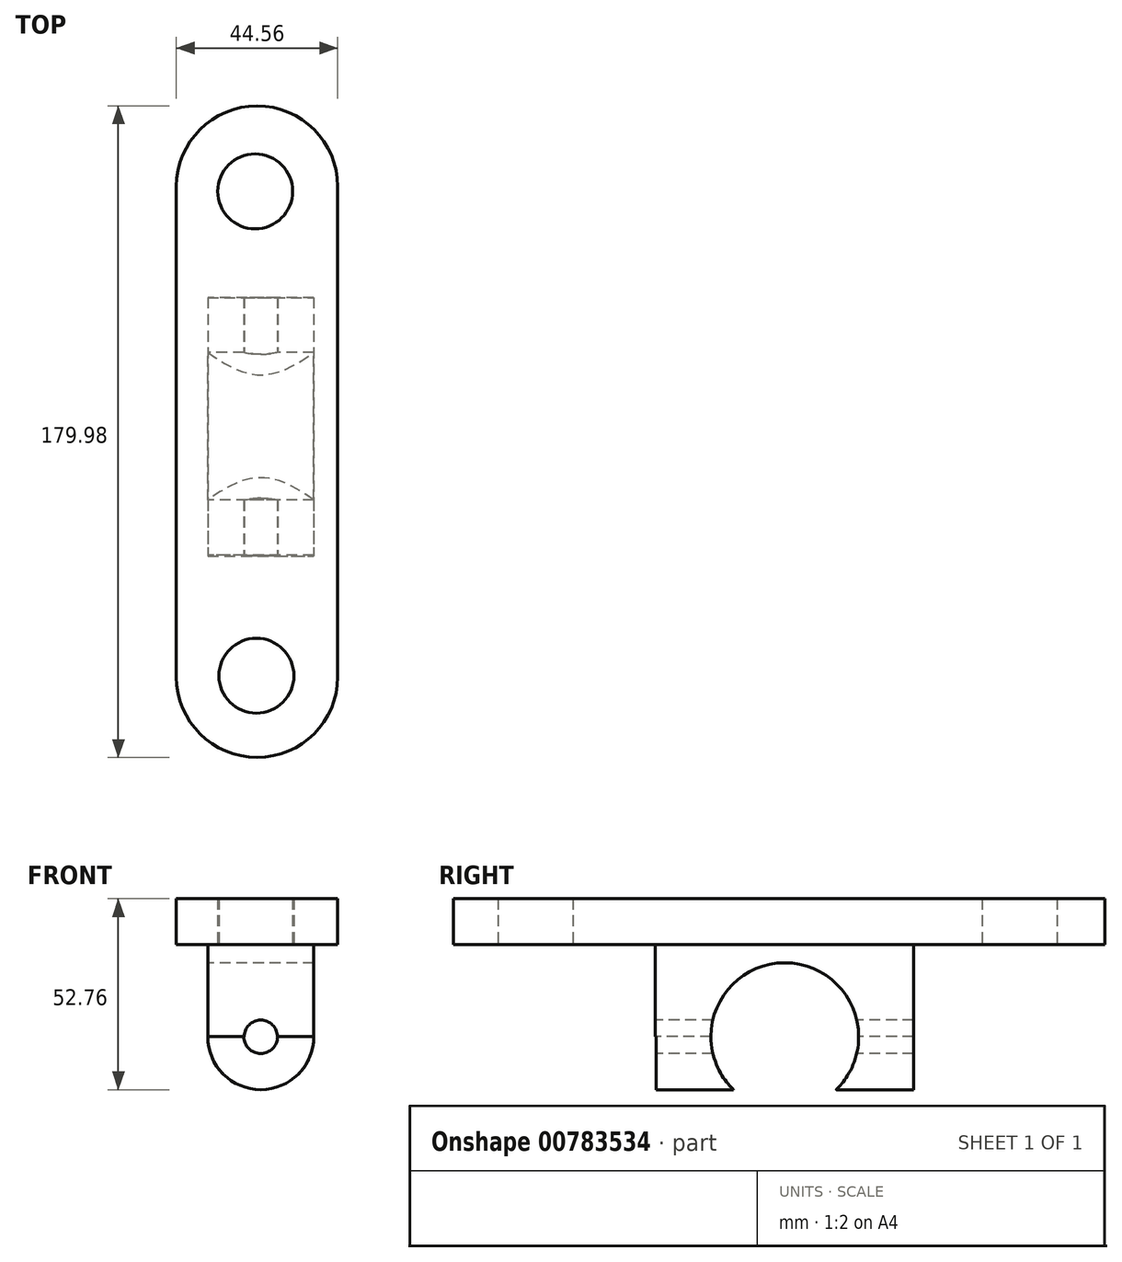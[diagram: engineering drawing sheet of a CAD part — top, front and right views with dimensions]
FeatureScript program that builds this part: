
annotation { "Feature Type Name" : "Feature", "Feature Type Description" : "" }
export const myFeature = defineFeature(function(context is Context, id is Id, definition is map)
    precondition{}
    {
        {
            var Q0;
            Q0=qCreatedBy(makeId("Top.planeOp"),FACE);
            var sketch = newSketch(context, id + "F0", { "sketchPlane" : qUnion([Q0])});
            skLineSegment(sketch, "E0.bottom", {"start": v(-28.13, -64.81) * mm, "end": v(16.43, -64.81) * mm});
            skLineSegment(sketch, "E0.top", {"start": v(-28.13, 70.6) * mm, "end": v(16.43, 70.6) * mm});
            skLineSegment(sketch, "E0.left", {"start": v(-28.13, -64.81) * mm, "end": v(-28.13, 70.6) * mm});
            skLineSegment(sketch, "E0.right", {"start": v(16.43, -64.81) * mm, "end": v(16.43, 70.6) * mm});
            skCircle(sketch, "E1", {"center": v(-5.85, 70.6) * mm, "radius": 22.28 * mm});
            skCircle(sketch, "E2", {"center": v(-5.85, -64.81) * mm, "radius": 22.28 * mm});
            skSolve(sketch);
        }
        {
            var Q0;
            {var subQ0=sQuery(id+"F0.wireOp",EDGE,"E0.left");Q0=makeQuery(id+"F0.imprint","IMPRINT",FACE,{"disambiguationData":[TD([[makeQuery(id+"F0.imprint","IMPRINT",EDGE,{"derivedFrom":subQ0}),-1.0]])]});}
            var Q1;
            {var subQ0=sQuery(id+"F0.wireOp",EDGE,"E0.top");Q1=makeQuery(id+"F0.imprint","IMPRINT",FACE,{"disambiguationData":[TD([[makeQuery(id+"F0.imprint","IMPRINT",EDGE,{"derivedFrom":subQ0}),-1.0]])]});}
            var Q2;
            {var subQ0=sQuery(id+"F0.wireOp",EDGE,"E0.top");Q2=makeQuery(id+"F0.imprint","IMPRINT",FACE,{"disambiguationData":[TD([[makeQuery(id+"F0.imprint","IMPRINT",EDGE,{"derivedFrom":subQ0}),1.0]])]});}
            var Q3;
            {var subQ0=sQuery(id+"F0.wireOp",EDGE,"E0.bottom");Q3=makeQuery(id+"F0.imprint","IMPRINT",FACE,{"disambiguationData":[TD([[makeQuery(id+"F0.imprint","IMPRINT",EDGE,{"derivedFrom":subQ0}),-1.0]])]});}
            var Q4;
            {var subQ0=sQuery(id+"F0.wireOp",EDGE,"E0.bottom");Q4=makeQuery(id+"F0.imprint","IMPRINT",FACE,{"disambiguationData":[TD([[makeQuery(id+"F0.imprint","IMPRINT",EDGE,{"derivedFrom":subQ0}),1.0]])]});}
            extrude(context, id + "F1", {"entities" : qUnion([Q0, Q1, Q2, Q3, Q4]), "depth" : 12.7 * mm, "offsetDistance" : 25.4 * mm});
        }
        {
            var Q0;
            Q0=qCreatedBy(makeId("Top.planeOp"),FACE);
            var sketch = newSketch(context, id + "F2", { "sketchPlane" : qUnion([Q0])});
            skCircle(sketch, "E3", {"center": v(-6.38, 69.27) * mm, "radius": 10.35 * mm});
            skCircle(sketch, "E4", {"center": v(-6.03, -64.52) * mm, "radius": 10.35 * mm});
            skSolve(sketch);
        }
        {
            var Q0;
            Q0=makeQuery(id+"F2.imprint","IMPRINT",FACE,{"disambiguationData":[TD([[makeQuery(id+"F2.imprint","IMPRINT",EDGE,{"derivedFrom":sQuery(id+"F2.wireOp",EDGE,"E3")}),1.0]])]});
            var Q1;
            Q1=makeQuery(id+"F2.imprint","IMPRINT",FACE,{"disambiguationData":[TD([[makeQuery(id+"F2.imprint","IMPRINT",EDGE,{"derivedFrom":sQuery(id+"F2.wireOp",EDGE,"E4")}),1.0]])]});
            extrude(context, id + "F3", {"entities" : qUnion([Q0, Q1]), "operationType" : NewBodyOperationType.REMOVE, "depth" : 12.7 * mm, "offsetDistance" : 25.4 * mm});
        }
        {
            var Q0;
            Q0=qCreatedBy(makeId("Top.planeOp"),FACE);
            var sketch = newSketch(context, id + "F4", { "sketchPlane" : qUnion([Q0])});
            skLineSegment(sketch, "E5.bottom", {"start": v(-19.48, 39.96) * mm, "end": v(9.83, 39.96) * mm});
            skLineSegment(sketch, "E5.top", {"start": v(-19.48, -31.42) * mm, "end": v(9.83, -31.42) * mm});
            skLineSegment(sketch, "E5.left", {"start": v(-19.48, 39.96) * mm, "end": v(-19.48, -31.42) * mm});
            skLineSegment(sketch, "E5.right", {"start": v(9.83, 39.96) * mm, "end": v(9.83, -31.42) * mm});
            skSolve(sketch);
        }
        {
            var Q0;
            Q0=makeQuery(id+"F4.imprint","IMPRINT",FACE,{"disambiguationData":[TD([[makeQuery(id+"F4.imprint","IMPRINT",EDGE,{"derivedFrom":sQuery(id+"F4.wireOp",EDGE,"E5.bottom")}),-1.0]])]});
            extrude(context, id + "F5", {"entities" : qUnion([Q0]), "operationType" : NewBodyOperationType.ADD, "oppositeDirection" : true, "depth" : 25.4 * mm, "offsetDistance" : 25.4 * mm});
        }
        {
            var Q0;
            Q0=makeQuery(id+"F5.opExtrude","SWEPT_FACE",FACE,{"disambiguationData":[OSD([sQuery(id+"F4.wireOp",EDGE,"E5.bottom")])]});
            var sketch = newSketch(context, id + "F6", { "sketchPlane" : qUnion([Q0])});
            skCircle(sketch, "E6", {"center": v(4.83, -25.4) * mm, "radius": 14.66 * mm});
            skSolve(sketch);
        }
        {
            var Q0;
            {var subQ1=sQuery(id+"F4.wireOp",EDGE,"E5.bottom");var subQ2=makeQuery(id+"F5.opExtrude","CAP_EDGE",EDGE,{"disambiguationData":[OSD([subQ1])],"isStart":false});Q0=makeQuery(id+"F6.imprint","IMPRINT",FACE,{"disambiguationData":[TD([[makeQuery(id+"F6.imprint","IMPRINT",EDGE,{"derivedFrom":subQ2}),1.0]])]});}
            var Q1;
            {var subQ1=sQuery(id+"F4.wireOp",EDGE,"E5.bottom");var subQ2=makeQuery(id+"F5.opExtrude","CAP_EDGE",EDGE,{"disambiguationData":[OSD([subQ1])],"isStart":false});Q1=makeQuery(id+"F6.imprint","IMPRINT",FACE,{"disambiguationData":[TD([[makeQuery(id+"F6.imprint","IMPRINT",EDGE,{"derivedFrom":subQ2}),-1.0]])]});}
            extrude(context, id + "F7", {"entities" : qUnion([Q0, Q1]), "operationType" : NewBodyOperationType.ADD, "oppositeDirection" : true, "depth" : 71.12 * mm, "offsetDistance" : 25.4 * mm});
        }
        {
            var Q0;
            Q0=makeQuery(id+"F5.opExtrude","SWEPT_FACE",FACE,{"disambiguationData":[OSD([sQuery(id+"F4.wireOp",EDGE,"E5.left")])]});
            var sketch = newSketch(context, id + "F8", { "sketchPlane" : qUnion([Q0])});
            skCircle(sketch, "E7", {"center": v(-4.4, -25.4) * mm, "radius": 20.4 * mm});
            skSolve(sketch);
        }
        {
            var Q0;
            {var subQ0=sQuery(id+"F8.wireOp",EDGE,"E7");var subQ1=sQuery(id+"F4.wireOp",EDGE,"E5.left");var subQ2=makeQuery(id+"F7.boolean.opBoolean","SPLIT",EDGE,{"disambiguationData":[topologyDisambiguationEdgeConnected([makeQuery(id+"F7.opExtrude","SWEPT_FACE",FACE,{"disambiguationData":[OSD([sQuery(id+"F6.wireOp",EDGE,"E6")])]})])],"derivedFrom":makeQuery(id+"F5.opExtrude","CAP_EDGE",EDGE,{"disambiguationData":[OSD([subQ1])],"isStart":false})});var subQ3=makeQuery(id+"F8.imprint","INTERSECT",VERTEX,{"disambiguationData":[OD(0.0)],"derivedFrom":[subQ2,subQ0]});Q0=makeQuery(id+"F8.imprint","IMPRINT",FACE,{"disambiguationData":[TD([[makeQuery(id+"F8.imprint","IMPRINT",EDGE,{"disambiguationData":[TD([[subQ3,-1.0]])],"derivedFrom":subQ0}),1.0]])]});}
            var Q1;
            {var subQ0=sQuery(id+"F8.wireOp",EDGE,"E7");var subQ1=sQuery(id+"F4.wireOp",EDGE,"E5.left");var subQ2=makeQuery(id+"F7.boolean.opBoolean","SPLIT",EDGE,{"disambiguationData":[topologyDisambiguationEdgeConnected([makeQuery(id+"F7.opExtrude","SWEPT_FACE",FACE,{"disambiguationData":[OSD([sQuery(id+"F6.wireOp",EDGE,"E6")])]})])],"derivedFrom":makeQuery(id+"F5.opExtrude","CAP_EDGE",EDGE,{"disambiguationData":[OSD([subQ1])],"isStart":false})});var subQ3=makeQuery(id+"F8.imprint","INTERSECT",VERTEX,{"disambiguationData":[OD(0.0)],"derivedFrom":[subQ2,subQ0]});Q1=makeQuery(id+"F8.imprint","IMPRINT",FACE,{"disambiguationData":[TD([[makeQuery(id+"F8.imprint","IMPRINT",EDGE,{"disambiguationData":[TD([[subQ3,1.0]])],"derivedFrom":subQ0}),1.0]])]});}
            extrude(context, id + "F9", {"entities" : qUnion([Q0, Q1]), "operationType" : NewBodyOperationType.REMOVE, "oppositeDirection" : true, "depth" : 30.48 * mm, "offsetDistance" : 25.4 * mm});
        }
        {
            var Q0;
            Q0=makeQuery(id+"F7.opExtrude","CAP_FACE",FACE,{"disambiguationData":[OSD([sQuery(id+"F6.wireOp",EDGE,"E6")])],"isStart":false});
            var sketch = newSketch(context, id + "F10", { "sketchPlane" : qUnion([Q0])});
            skCircle(sketch, "E8", {"center": v(-4.83, -25.4) * mm, "radius": 4.67 * mm});
            skSolve(sketch);
        }
        {
            var Q0;
            {var subQ0=sQuery(id+"F10.wireOp",EDGE,"E8");var subQ1=makeQuery(id+"F7.boolean.opBoolean","INTERSECT",EDGE,{"derivedFrom":[makeQuery(id+"F5.opExtrude","CAP_FACE",FACE,{"disambiguationData":[OSD([sQuery(id+"F4.wireOp",EDGE,"E5.bottom"),sQuery(id+"F4.wireOp",EDGE,"E5.top"),sQuery(id+"F4.wireOp",EDGE,"E5.left"),sQuery(id+"F4.wireOp",EDGE,"E5.right")])],"isStart":false}),makeQuery(id+"F7.opExtrude","CAP_FACE",FACE,{"disambiguationData":[OSD([sQuery(id+"F6.wireOp",EDGE,"E6")])],"isStart":false})]});var subQ2=makeQuery(id+"F10.imprint","INTERSECT",VERTEX,{"disambiguationData":[OD(0.0)],"derivedFrom":[subQ1,subQ0]});Q0=makeQuery(id+"F10.imprint","IMPRINT",FACE,{"disambiguationData":[TD([[makeQuery(id+"F10.imprint","IMPRINT",EDGE,{"disambiguationData":[TD([[subQ2,-1.0]])],"derivedFrom":subQ0}),1.0]])]});}
            extrude(context, id + "F11", {"entities" : qUnion([Q0]), "operationType" : NewBodyOperationType.REMOVE, "oppositeDirection" : true, "depth" : 101.6 * mm, "offsetDistance" : 25.4 * mm});
        }
        {
            var Q0;
            Q0=makeQuery(id+"F5.opExtrude","SWEPT_FACE",FACE,{"disambiguationData":[OSD([sQuery(id+"F4.wireOp",EDGE,"E5.top")])]});
            var sketch = newSketch(context, id + "F12", { "sketchPlane" : qUnion([Q0])});
            skCircle(sketch, "E9", {"center": v(-4.83, -25.4) * mm, "radius": 4.57 * mm});
            skSolve(sketch);
        }
        {
            var Q0;
            {var subQ0=sQuery(id+"F12.wireOp",EDGE,"E9");var subQ1=makeQuery(id+"F5.opExtrude","CAP_EDGE",EDGE,{"disambiguationData":[OSD([sQuery(id+"F4.wireOp",EDGE,"E5.top")])],"isStart":false});var subQ2=makeQuery(id+"F12.imprint","INTERSECT",VERTEX,{"disambiguationData":[OD(0.0)],"derivedFrom":[subQ1,subQ0]});Q0=makeQuery(id+"F12.imprint","IMPRINT",FACE,{"disambiguationData":[TD([[makeQuery(id+"F12.imprint","IMPRINT",EDGE,{"disambiguationData":[TD([[subQ2,1.0]])],"derivedFrom":subQ0}),1.0]])]});}
            extrude(context, id + "F13", {"entities" : qUnion([Q0]), "operationType" : NewBodyOperationType.REMOVE, "oppositeDirection" : true, "depth" : 101.6 * mm, "offsetDistance" : 25.4 * mm});
        }
    });
